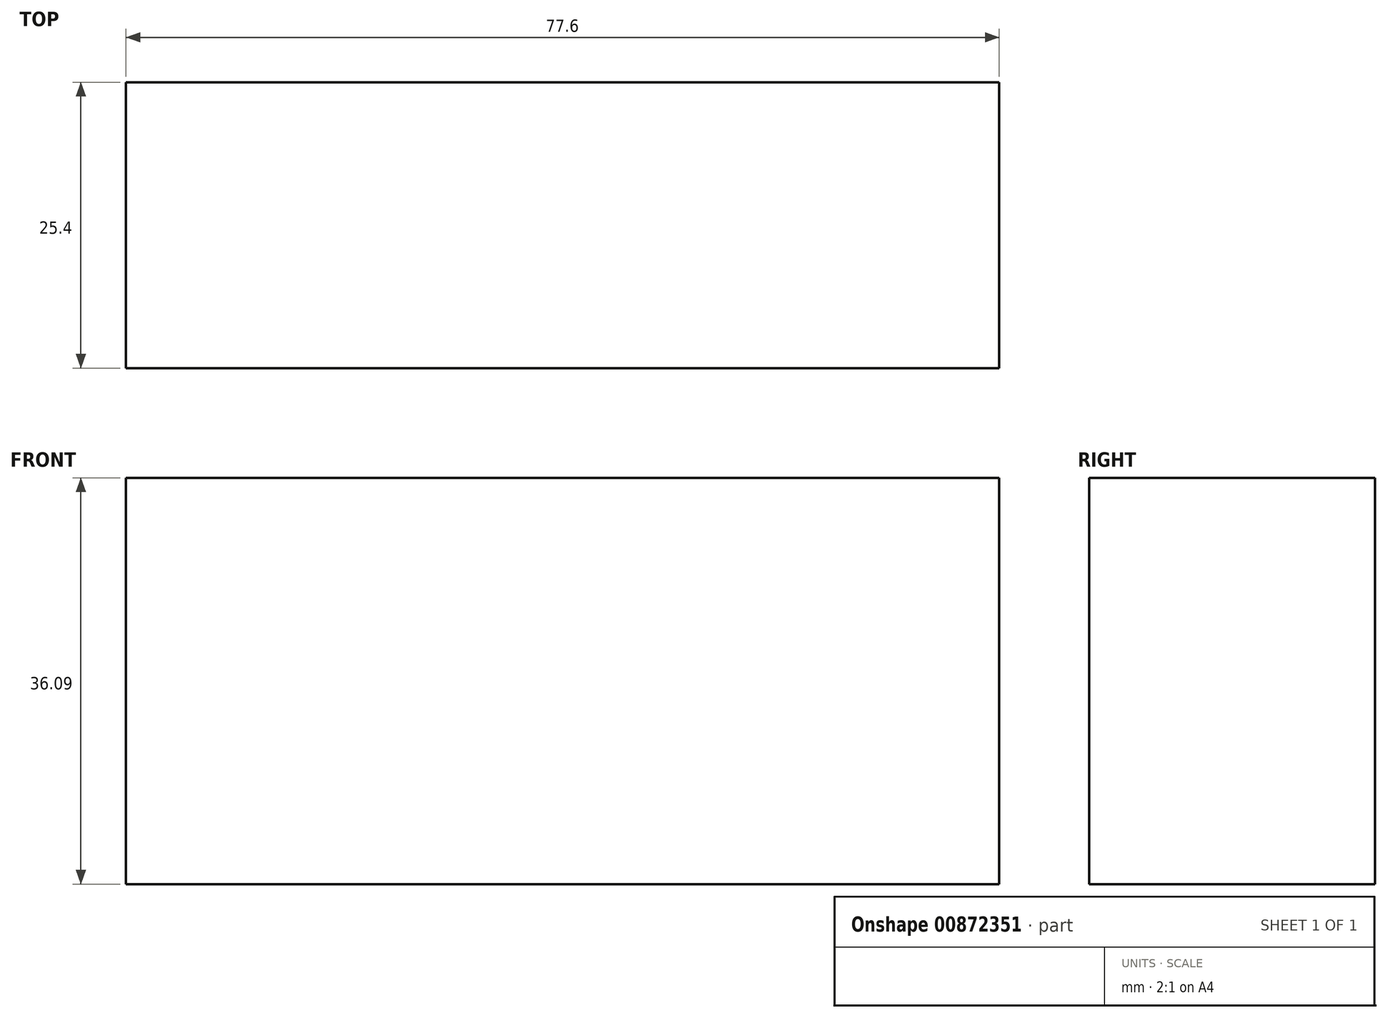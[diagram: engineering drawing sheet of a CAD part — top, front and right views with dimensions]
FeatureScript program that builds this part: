
annotation { "Feature Type Name" : "Feature", "Feature Type Description" : "" }
export const myFeature = defineFeature(function(context is Context, id is Id, definition is map)
    precondition{}
    {
        {
            var Q0;
            Q0=qCreatedBy(makeId("Front.planeOp"),FACE);
            var sketch = newSketch(context, id + "F0", { "sketchPlane" : qUnion([Q0])});
            skLineSegment(sketch, "E0.bottom", {"start": v(-30.83, -5.56) * mm, "end": v(46.77, -5.56) * mm});
            skLineSegment(sketch, "E0.top", {"start": v(-30.83, 30.53) * mm, "end": v(46.77, 30.53) * mm});
            skLineSegment(sketch, "E0.left", {"start": v(-30.83, -5.56) * mm, "end": v(-30.83, 30.53) * mm});
            skLineSegment(sketch, "E0.right", {"start": v(46.77, -5.56) * mm, "end": v(46.77, 30.53) * mm});
            skSolve(sketch);
        }
        {
            var Q0;
            Q0 = qSketchRegion(id + "F0", true);
            extrude(context, id + "F1", {"entities" : qUnion([Q0]), "depth" : 25.4 * mm, "offsetDistance" : 25.4 * mm});
        }
    });
